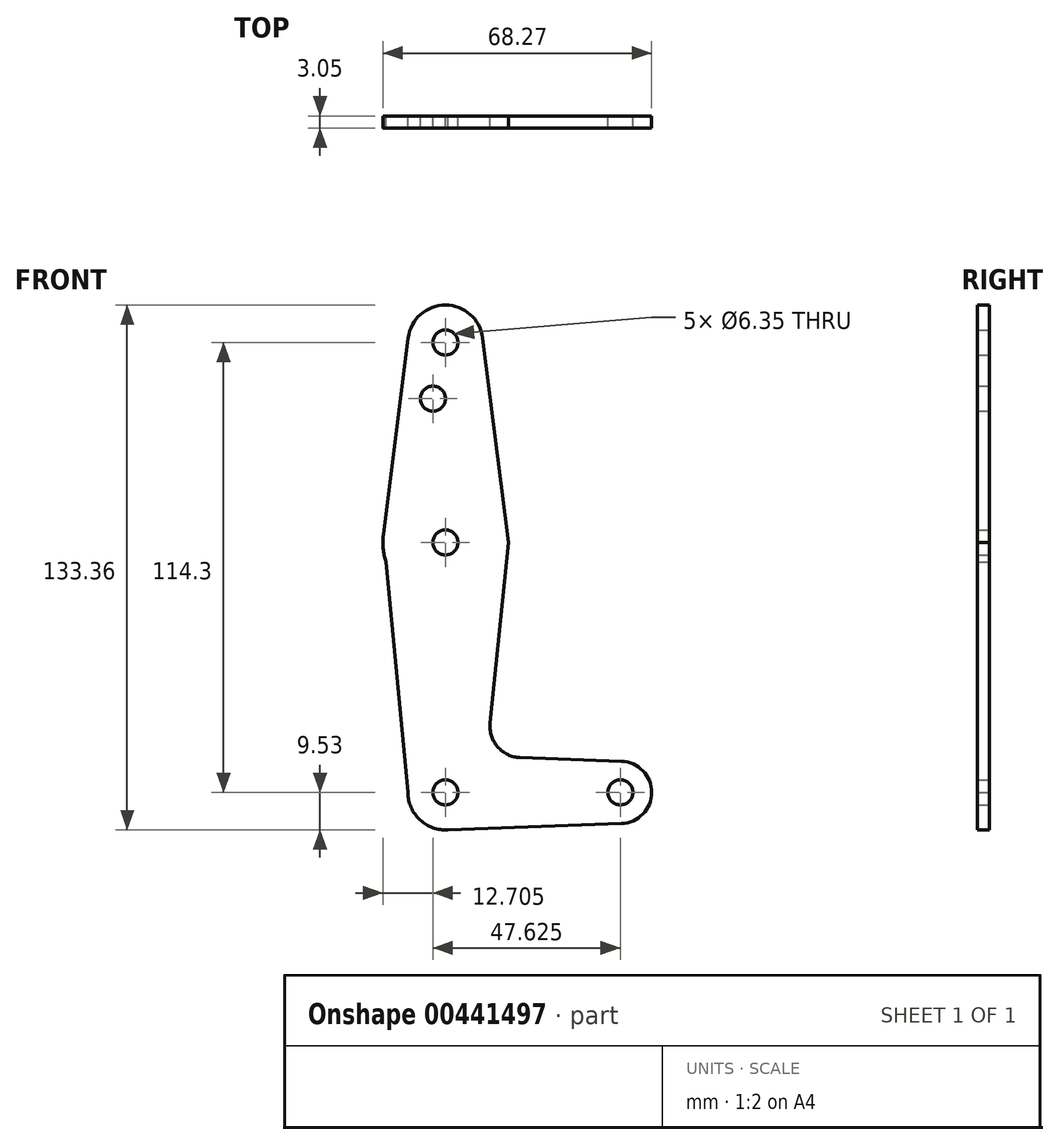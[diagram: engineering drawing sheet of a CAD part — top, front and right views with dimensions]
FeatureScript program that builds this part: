
annotation { "Feature Type Name" : "Feature", "Feature Type Description" : "" }
export const myFeature = defineFeature(function(context is Context, id is Id, definition is map)
    precondition{}
    {
        {
            var Q0;
            Q0=qCreatedBy(makeId("Front.planeOp"),FACE);
            var sketch = newSketch(context, id + "F0", { "sketchPlane" : qUnion([Q0])});
            skLineSegment(sketch, "E0", {"start": v(0, 0) * mm, "end": v(0, 114.3) * mm, "construction": true});
            skLineSegment(sketch, "E1", {"start": v(0, 0) * mm, "end": v(44.45, 0) * mm, "construction": true});
            skCircle(sketch, "E2", {"center": v(0, 114.3) * mm, "radius": 9.53 * mm});
            skCircle(sketch, "E3", {"center": v(0, 63.5) * mm, "radius": 15.88 * mm});
            skCircle(sketch, "E4", {"center": v(0, 0) * mm, "radius": 9.53 * mm});
            skCircle(sketch, "E5", {"center": v(44.45, 0) * mm, "radius": 7.94 * mm});
            skLineSegment(sketch, "E6", {"start": v(-9.45, 115.5) * mm, "end": v(-15.75, 65.48) * mm});
            skLineSegment(sketch, "E7", {"start": v(-9.53, 0) * mm, "end": v(-15.75, 65.48) * mm});
            skLineSegment(sketch, "E8", {"start": v(9.45, 115.5) * mm, "end": v(16, 63.5) * mm});
            skLineSegment(sketch, "E9", {"start": v(16, 63.5) * mm, "end": v(11.35, 17.6) * mm});
            skCircle(sketch, "E10", {"center": v(0, 114.3) * mm, "radius": 3.18 * mm});
            skCircle(sketch, "E11", {"center": v(0, 63.5) * mm, "radius": 3.18 * mm});
            skCircle(sketch, "E12", {"center": v(0, 0) * mm, "radius": 3.18 * mm});
            skCircle(sketch, "E13", {"center": v(44.45, 0) * mm, "radius": 3.18 * mm});
            skCircle(sketch, "E14", {"center": v(-3.18, 100.03) * mm, "radius": 3.18 * mm});
            skLineSegment(sketch, "E15", {"start": v(18.98, 8.85) * mm, "end": v(44.73, 7.93) * mm});
            skLineSegment(sketch, "E16", {"start": v(0, -9.53) * mm, "end": v(44.73, -7.93) * mm});
            skPoint(sketch, "E17.newPointB", {"position": v(0, 9.53) * mm});
            skArc(sketch, "E17.filletArc", {"start": v(11.35, 17.6) * mm, "mid": v(13.27, 11.57) * mm, "end": v(18.98, 8.85) * mm});
            skSolve(sketch);
        }
        {
            var Q0;
            Q0 = qSketchRegion(id + "F0", true);
            extrude(context, id + "F1", {"entities" : qUnion([Q0]), "depth" : 3.05 * mm});
        }
    });
